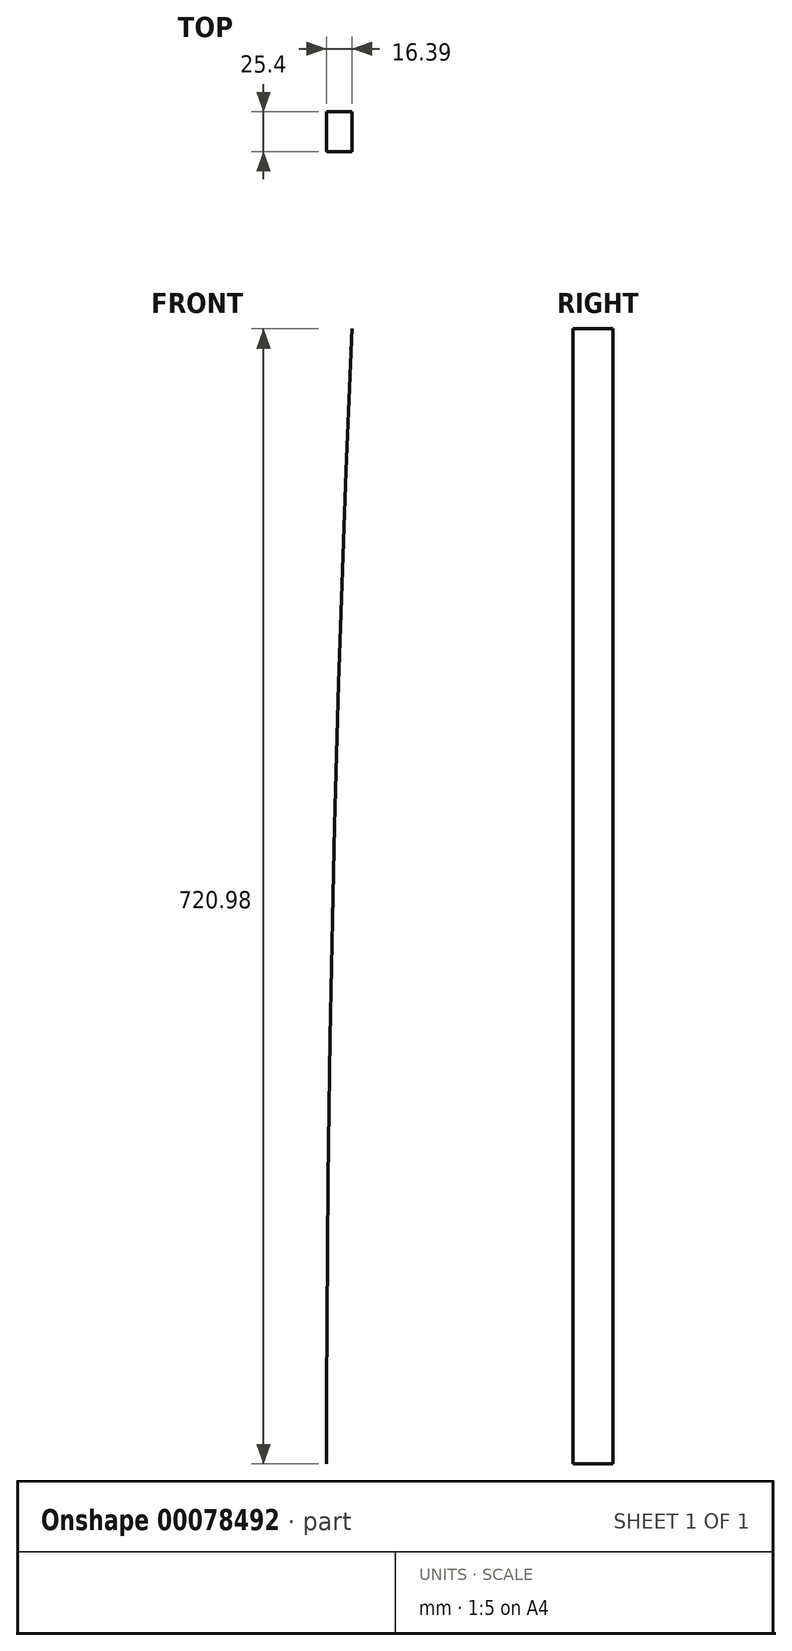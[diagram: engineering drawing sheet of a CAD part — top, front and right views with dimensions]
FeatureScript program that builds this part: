
annotation { "Feature Type Name" : "Feature", "Feature Type Description" : "" }
export const myFeature = defineFeature(function(context is Context, id is Id, definition is map)
    precondition{}
    {
        {
            var Q0;
            Q0=qCreatedBy(makeId("Front.planeOp"),FACE);
            var sketch = newSketch(context, id + "F0", { "sketchPlane" : qUnion([Q0])});
            skLineSegment(sketch, "E0.bottom", {"start": v(-41.27, -9.53) * mm, "end": v(41.28, -9.53) * mm});
            skLineSegment(sketch, "E0.top", {"start": v(-41.28, 9.52) * mm, "end": v(41.28, 9.52) * mm});
            skLineSegment(sketch, "E0.left", {"start": v(-41.28, -9.53) * mm, "end": v(-41.28, 9.52) * mm});
            skLineSegment(sketch, "E0.right", {"start": v(41.28, -9.53) * mm, "end": v(41.28, 9.52) * mm});
            skPoint(sketch, "E0.middle", {"position": v(0, 0) * mm});
            skLineSegment(sketch, "E1.bottom", {"start": v(50.65, 23.73) * mm, "end": v(101.45, 23.73) * mm});
            skLineSegment(sketch, "E1.top", {"start": v(50.65, 52.3) * mm, "end": v(101.45, 52.3) * mm});
            skLineSegment(sketch, "E1.left", {"start": v(50.65, 23.73) * mm, "end": v(50.65, 52.3) * mm});
            skLineSegment(sketch, "E1.right", {"start": v(101.45, 23.73) * mm, "end": v(101.45, 52.3) * mm});
            skPoint(sketch, "E1.middle", {"position": v(76.05, 38.02) * mm});
            skLineSegment(sketch, "E2", {"start": v(41.28, -682.96) * mm, "end": v(41.28, 9.52) * mm});
            skArc(sketch, "E3", {"start": v(41.28, -682.96) * mm, "mid": v(45.37, -322.38) * mm, "end": v(57.66, 38.02) * mm});
            skPoint(sketch, "E3.endSnap0", {"position": v(50.65, 38.02) * mm});
            skLineSegment(sketch, "E4", {"start": v(57.66, 38.02) * mm, "end": v(87.71, 38.02) * mm});
            skSolve(sketch);
        }
        {
            var Q0;
            Q0=sQuery(id+"F0.wireOp",EDGE,"E3");
            extrude(context, id + "F1", {"bodyType" : ToolBodyType.SURFACE, "surfaceEntities" : qUnion([Q0]), "depth" : 25.4 * mm});
        }
    });
